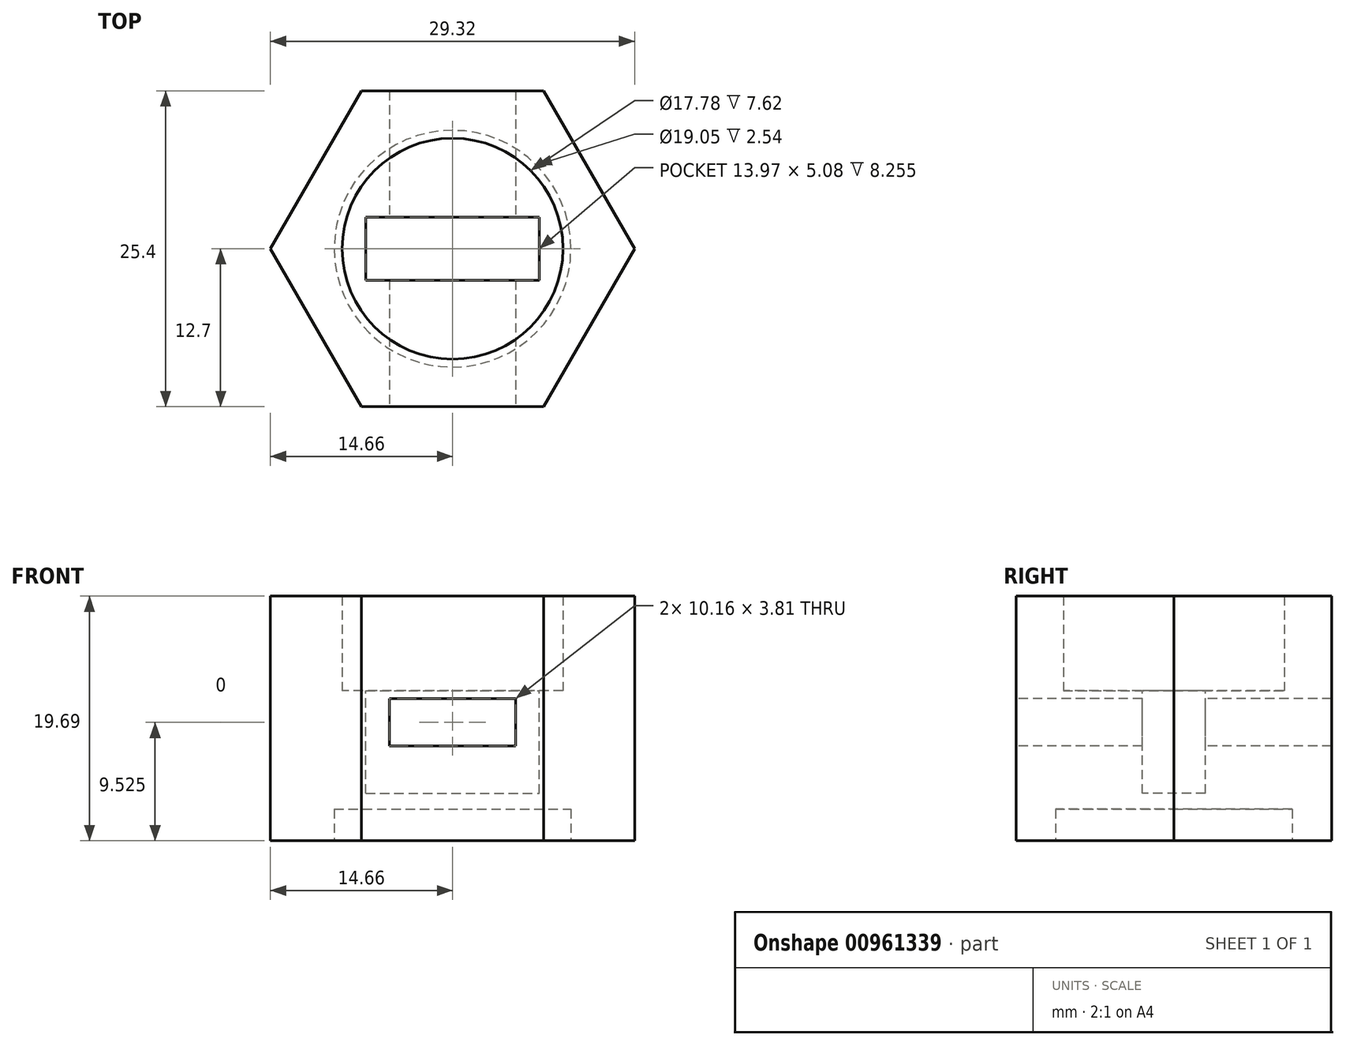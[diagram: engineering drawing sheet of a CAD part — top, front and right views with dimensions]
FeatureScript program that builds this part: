
annotation { "Feature Type Name" : "Feature", "Feature Type Description" : "" }
export const myFeature = defineFeature(function(context is Context, id is Id, definition is map)
    precondition{}
    {
        {
            var Q0;
            Q0=qCreatedBy(makeId("Top.planeOp"),FACE);
            var sketch = newSketch(context, id + "F0", { "sketchPlane" : qUnion([Q0])});
            skCircle(sketch, "E0.cCircle", {"center": v(0, 0) * mm, "radius": 14.66 * mm, "construction": true});
            skLineSegment(sketch, "E0.0", {"start": v(14.66, 0) * mm, "end": v(7.33, -12.7) * mm});
            skLineSegment(sketch, "E0.1", {"start": v(7.33, -12.7) * mm, "end": v(-7.33, -12.7) * mm});
            skLineSegment(sketch, "E0.2", {"start": v(-7.33, -12.7) * mm, "end": v(-14.66, 0) * mm});
            skLineSegment(sketch, "E0.3", {"start": v(-14.66, 0) * mm, "end": v(-7.33, 12.7) * mm});
            skLineSegment(sketch, "E0.4", {"start": v(-7.33, 12.7) * mm, "end": v(7.33, 12.7) * mm});
            skLineSegment(sketch, "E0.5", {"start": v(7.33, 12.7) * mm, "end": v(14.66, 0) * mm});
            skSolve(sketch);
        }
        {
            var Q0;
            Q0 = qSketchRegion(id + "F0", true);
            extrude(context, id + "F1", {"entities" : qUnion([Q0]), "depth" : 12.06 * mm, "offsetDistance" : 25.4 * mm});
        }
        {
            var Q0;
            Q0=makeQuery(id+"F1.opExtrude","SWEPT_FACE",FACE,{"disambiguationData":[OSD([sQuery(id+"F0.wireOp",EDGE,"E0.1")])]});
            var sketch = newSketch(context, id + "F2", { "sketchPlane" : qUnion([Q0])});
            skLineSegment(sketch, "E1.bottom", {"start": v(-5.08, 11.43) * mm, "end": v(5.08, 11.43) * mm});
            skLineSegment(sketch, "E1.top", {"start": v(-5.08, 7.62) * mm, "end": v(5.08, 7.62) * mm});
            skLineSegment(sketch, "E1.left", {"start": v(-5.08, 11.43) * mm, "end": v(-5.08, 7.62) * mm});
            skLineSegment(sketch, "E1.right", {"start": v(5.08, 11.43) * mm, "end": v(5.08, 7.62) * mm});
            skSolve(sketch);
        }
        {
            var Q0;
            Q0=makeQuery(id+"F2.imprint","IMPRINT",FACE,{"disambiguationData":[TD([[makeQuery(id+"F2.imprint","IMPRINT",EDGE,{"derivedFrom":sQuery(id+"F2.wireOp",EDGE,"E1.bottom")}),-1.0]])]});
            var Q1;
            Q1 = qSketchRegion(id + "F4", true);
            extrude(context, id + "F3", {"entities" : qUnion([Q0, Q1]), "operationType" : NewBodyOperationType.REMOVE, "endBound" : BoundingType.THROUGH_ALL, "oppositeDirection" : true, "depth" : 25.4 * mm, "offsetDistance" : 25.4 * mm});
        }
        {
            var Q0;
            Q0=makeQuery(id+"F1.opExtrude","CAP_FACE",FACE,{"disambiguationData":[OSD([sQuery(id+"F0.wireOp",EDGE,"E0.0"),sQuery(id+"F0.wireOp",EDGE,"E0.1"),sQuery(id+"F0.wireOp",EDGE,"E0.2"),sQuery(id+"F0.wireOp",EDGE,"E0.3"),sQuery(id+"F0.wireOp",EDGE,"E0.4"),sQuery(id+"F0.wireOp",EDGE,"E0.5")])],"isStart":false});
            var sketch = newSketch(context, id + "F4", { "sketchPlane" : qUnion([Q0])});
            skCircle(sketch, "E2", {"center": v(0, 0) * mm, "radius": 8.89 * mm});
            skSolve(sketch);
        }
        {
            var Q0;
            Q0=makeQuery(id+"F4.imprint","IMPRINT",FACE,{"disambiguationData":[TD([[makeQuery(id+"F4.imprint","IMPRINT",EDGE,{"derivedFrom":sQuery(id+"F4.wireOp",EDGE,"E2")}),-1.0]])]});
            var sketch = newSketch(context, id + "F5", { "sketchPlane" : qUnion([Q0])});
            skLineSegment(sketch, "E3.bottom", {"start": v(-6.99, 2.54) * mm, "end": v(6.99, 2.54) * mm});
            skLineSegment(sketch, "E3.top", {"start": v(-6.99, -2.54) * mm, "end": v(6.99, -2.54) * mm});
            skLineSegment(sketch, "E3.left", {"start": v(-6.99, 2.54) * mm, "end": v(-6.99, -2.54) * mm});
            skLineSegment(sketch, "E3.right", {"start": v(6.99, 2.54) * mm, "end": v(6.99, -2.54) * mm});
            skSolve(sketch);
        }
        {
            var Q0;
            Q0=makeQuery(id+"F5.imprint","IMPRINT",FACE,{"disambiguationData":[TD([[makeQuery(id+"F5.imprint","IMPRINT",EDGE,{"derivedFrom":sQuery(id+"F5.wireOp",EDGE,"E3.bottom")}),-1.0]])]});
            extrude(context, id + "F6", {"entities" : qUnion([Q0]), "operationType" : NewBodyOperationType.REMOVE, "oppositeDirection" : true, "depth" : 8.25 * mm, "offsetDistance" : 25.4 * mm});
        }
        {
            var Q0;
            Q0=makeQuery(id+"F4.imprint","IMPRINT",FACE,{"disambiguationData":[TD([[makeQuery(id+"F4.imprint","IMPRINT",EDGE,{"derivedFrom":sQuery(id+"F4.wireOp",EDGE,"E2")}),-1.0]])]});
            extrude(context, id + "F7", {"entities" : qUnion([Q0]), "operationType" : NewBodyOperationType.ADD, "depth" : 7.62 * mm, "offsetDistance" : 25.4 * mm});
        }
        {
            var Q0;
            Q0=makeQuery(id+"F1.opExtrude","CAP_FACE",FACE,{"disambiguationData":[OSD([sQuery(id+"F0.wireOp",EDGE,"E0.0"),sQuery(id+"F0.wireOp",EDGE,"E0.1"),sQuery(id+"F0.wireOp",EDGE,"E0.2"),sQuery(id+"F0.wireOp",EDGE,"E0.3"),sQuery(id+"F0.wireOp",EDGE,"E0.4"),sQuery(id+"F0.wireOp",EDGE,"E0.5")])],"isStart":true});
            var sketch = newSketch(context, id + "F8", { "sketchPlane" : qUnion([Q0])});
            skCircle(sketch, "E4", {"center": v(0, 0) * mm, "radius": 9.53 * mm});
            skSolve(sketch);
        }
        {
            var Q0;
            Q0=makeQuery(id+"F8.imprint","IMPRINT",FACE,{"disambiguationData":[TD([[makeQuery(id+"F8.imprint","IMPRINT",EDGE,{"derivedFrom":sQuery(id+"F8.wireOp",EDGE,"E4")}),1.0]])]});
            extrude(context, id + "F9", {"entities" : qUnion([Q0]), "operationType" : NewBodyOperationType.REMOVE, "oppositeDirection" : true, "depth" : 2.54 * mm, "offsetDistance" : 25.4 * mm});
        }
    });
